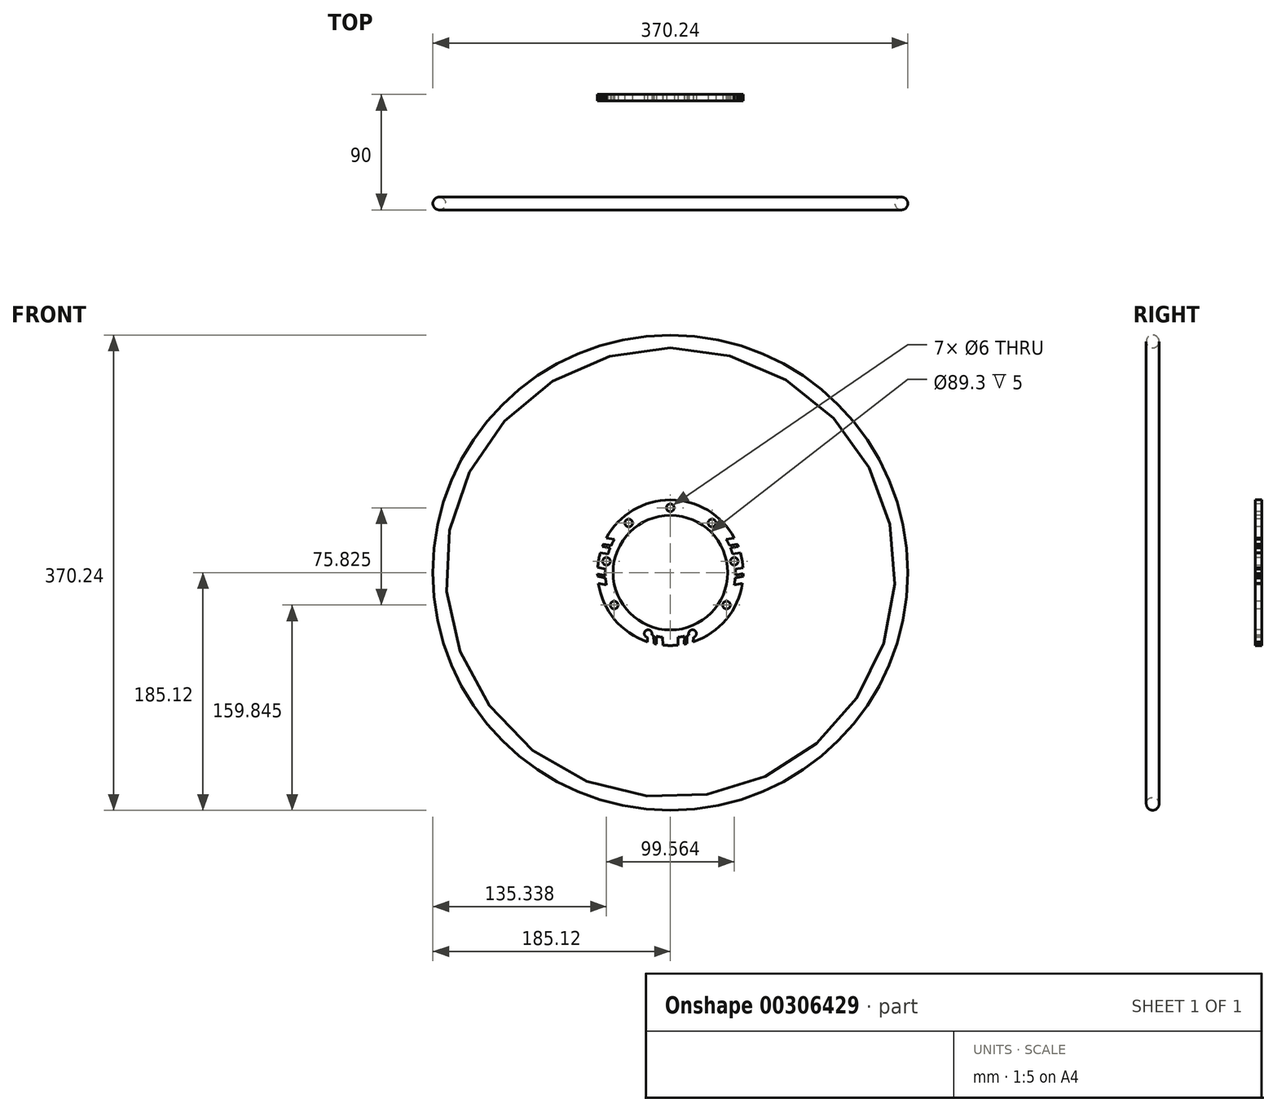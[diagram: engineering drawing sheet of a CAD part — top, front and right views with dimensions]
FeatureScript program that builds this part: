
annotation { "Feature Type Name" : "Feature", "Feature Type Description" : "" }
export const myFeature = defineFeature(function(context is Context, id is Id, definition is map)
    precondition{}
    {
        {
            var Q0;
            Q0=qCreatedBy(makeId("Front.planeOp"),FACE);
            var sketch = newSketch(context, id + "F0", { "sketchPlane" : qUnion([Q0])});
            skCircle(sketch, "E0", {"center": v(0, 0) * mm, "radius": 180 * mm});
            skCircle(sketch, "E1", {"center": v(0, 0) * mm, "radius": 44.65 * mm});
            skCircle(sketch, "E2", {"center": v(0, 50.55) * mm, "radius": 3 * mm});
            skCircle(sketch, "E3.1.0", {"center": v(32.5, 38.72) * mm, "radius": 3 * mm});
            skCircle(sketch, "E3.2.0", {"center": v(49.78, 8.78) * mm, "radius": 3 * mm});
            skLineSegment(sketch, "E3.anchor1", {"start": v(0, 0) * mm, "end": v(0, 50.55) * mm, "construction": true});
            skLineSegment(sketch, "E3.anchor2", {"start": v(0, 0) * mm, "end": v(-32.5, 38.72) * mm, "construction": true});
            skCircle(sketch, "E4.1.3.0", {"center": v(43.78, -25.28) * mm, "radius": 3 * mm});
            skCircle(sketch, "E4.1.4.0", {"center": v(17.29, -47.5) * mm, "radius": 3 * mm});
            skCircle(sketch, "E4.1.5.0", {"center": v(-17.29, -47.5) * mm, "radius": 3 * mm});
            skCircle(sketch, "E4.1.6.0", {"center": v(-43.78, -25.28) * mm, "radius": 3 * mm});
            skCircle(sketch, "E4.1.7.0", {"center": v(-49.78, 8.78) * mm, "radius": 3 * mm});
            skCircle(sketch, "E4.1.8.0", {"center": v(-32.5, 38.72) * mm, "radius": 3 * mm});
            skLineSegment(sketch, "E5", {"start": v(50.63, 2.67) * mm, "end": v(56.62, 3.9) * mm});
            skArc(sketch, "E6", {"start": v(-43.56, 25.94) * mm, "mid": v(-44.85, 23.65) * mm, "end": v(-46.01, 21.3) * mm});
            skArc(sketch, "E7.trimOffspring", {"start": v(-50.62, 2.76) * mm, "mid": v(-50.7, 0.27) * mm, "end": v(-50.65, -2.21) * mm});
            skArc(sketch, "E8.trimOffspring", {"start": v(-46.86, 19.36) * mm, "mid": v(-47.75, 17.04) * mm, "end": v(-48.53, 14.68) * mm});
            skArc(sketch, "E9.trimOffspring", {"start": v(-50.52, -4.32) * mm, "mid": v(-50.22, -6.93) * mm, "end": v(-49.8, -9.52) * mm});
            skArc(sketch, "E10", {"start": v(45.98, 21.35) * mm, "mid": v(44.82, 23.7) * mm, "end": v(43.53, 26) * mm});
            skArc(sketch, "E11.trimOffspring", {"start": v(50.66, -1.98) * mm, "mid": v(50.7, 0.34) * mm, "end": v(50.63, 2.67) * mm});
            skArc(sketch, "E12.trimOffspring", {"start": v(48.52, 14.7) * mm, "mid": v(47.73, 17.1) * mm, "end": v(46.81, 19.47) * mm});
            skArc(sketch, "E13.trimOffspring", {"start": v(49.81, -9.45) * mm, "mid": v(50.23, -6.86) * mm, "end": v(50.52, -4.25) * mm});
            skArc(sketch, "E14.trimOffspring", {"start": v(-14.5, -48.58) * mm, "mid": v(-13.75, -48.8) * mm, "end": v(-13, -49) * mm});
            skArc(sketch, "E15", {"start": v(6.06, -50.34) * mm, "mid": v(8.51, -49.98) * mm, "end": v(10.94, -49.5) * mm});
            skArc(sketch, "E16.trimOffspring", {"start": v(13, -49) * mm, "mid": v(13.75, -48.8) * mm, "end": v(14.5, -48.58) * mm});
            skArc(sketch, "E17.trimOffspring", {"start": v(-10.93, -49.5) * mm, "mid": v(-8.51, -49.98) * mm, "end": v(-6.07, -50.34) * mm});
            skLineSegment(sketch, "E18", {"start": v(44.82, 23.7) * mm, "end": v(174.77, 43.07) * mm});
            skLineSegment(sketch, "E19", {"start": v(47.73, 17.1) * mm, "end": v(176.31, 36.26) * mm});
            skLineSegment(sketch, "E20", {"start": v(50.7, 0.34) * mm, "end": v(178.06, 26.36) * mm});
            skLineSegment(sketch, "E21", {"start": v(50.23, -6.86) * mm, "end": v(178.95, 19.43) * mm});
            skLineSegment(sketch, "E22", {"start": v(8.51, -49.98) * mm, "end": v(5.15, -179.93) * mm});
            skLineSegment(sketch, "E23", {"start": v(-8.51, -49.98) * mm, "end": v(-5.41, -179.92) * mm});
            skLineSegment(sketch, "E24", {"start": v(15.36, -49.8) * mm, "end": v(12, -179.6) * mm});
            skLineSegment(sketch, "E25", {"start": v(-15.1, -49.55) * mm, "end": v(-12, -179.6) * mm});
            skLineSegment(sketch, "E26", {"start": v(-50.22, -6.93) * mm, "end": v(-178.89, 19.96) * mm});
            skLineSegment(sketch, "E27", {"start": v(-50.7, 0.27) * mm, "end": v(-177.98, 26.87) * mm});
            skLineSegment(sketch, "E28", {"start": v(-47.75, 17.04) * mm, "end": v(-176.2, 36.77) * mm});
            skPoint(sketch, "E29.startSnap0", {"position": v(-44.85, 23.65) * mm});
            skLineSegment(sketch, "E30", {"start": v(49.85, 27.12) * mm, "end": v(49.94, 26.95) * mm});
            skLineSegment(sketch, "E31", {"start": v(43.53, 26) * mm, "end": v(49.94, 26.95) * mm});
            skLineSegment(sketch, "E32", {"start": v(45.98, 21.35) * mm, "end": v(52.2, 22.28) * mm});
            skLineSegment(sketch, "E33", {"start": v(46.81, 19.47) * mm, "end": v(52.96, 20.38) * mm});
            skLineSegment(sketch, "E34", {"start": v(48.52, 14.7) * mm, "end": v(54.57, 15.6) * mm});
            skLineSegment(sketch, "E35", {"start": v(50.66, -1.98) * mm, "end": v(56.75, -0.74) * mm});
            skLineSegment(sketch, "E36", {"start": v(50.52, -4.25) * mm, "end": v(56.67, -3) * mm});
            skLineSegment(sketch, "E37", {"start": v(49.81, -9.45) * mm, "end": v(56.16, -8.15) * mm});
            skLineSegment(sketch, "E38", {"start": v(-43.56, 25.94) * mm, "end": v(-49.96, 26.92) * mm});
            skLineSegment(sketch, "E39", {"start": v(-46.01, 21.3) * mm, "end": v(-52.2, 22.24) * mm});
            skLineSegment(sketch, "E40", {"start": v(-46.86, 19.36) * mm, "end": v(-53, 20.3) * mm});
            skLineSegment(sketch, "E41", {"start": v(-48.53, 14.68) * mm, "end": v(-54.56, 15.6) * mm});
            skLineSegment(sketch, "E42", {"start": v(-50.65, -2.21) * mm, "end": v(-56.74, -0.94) * mm});
            skLineSegment(sketch, "E43", {"start": v(-50.62, 2.76) * mm, "end": v(-56.6, 4) * mm});
            skLineSegment(sketch, "E44", {"start": v(-50.52, -4.32) * mm, "end": v(-56.67, -3.03) * mm});
            skLineSegment(sketch, "E45", {"start": v(-49.8, -9.52) * mm, "end": v(-56.16, -8.2) * mm});
            skLineSegment(sketch, "E46", {"start": v(-44.85, 23.65) * mm, "end": v(-174.64, 43.58) * mm});
            skLineSegment(sketch, "E47", {"start": v(13, -49) * mm, "end": v(12.84, -55.28) * mm});
            skLineSegment(sketch, "E48", {"start": v(10.94, -49.5) * mm, "end": v(10.78, -55.72) * mm});
            skLineSegment(sketch, "E49", {"start": v(6.06, -50.34) * mm, "end": v(5.9, -56.44) * mm});
            skLineSegment(sketch, "E50", {"start": v(17.92, -50.43) * mm, "end": v(17.83, -53.88) * mm});
            skLineSegment(sketch, "E51", {"start": v(-6.07, -50.34) * mm, "end": v(-5.92, -56.44) * mm});
            skLineSegment(sketch, "E52", {"start": v(-10.93, -49.5) * mm, "end": v(-10.78, -55.72) * mm});
            skLineSegment(sketch, "E53", {"start": v(-13, -49) * mm, "end": v(-12.85, -55.28) * mm});
            skLineSegment(sketch, "E54", {"start": v(-17.92, -50.43) * mm, "end": v(-17.84, -53.87) * mm});
            skArc(sketch, "E55", {"start": v(49.94, 26.95) * mm, "mid": v(-0.02, 56.75) * mm, "end": v(-49.96, 26.92) * mm});
            skArc(sketch, "E56.trimOffspring", {"start": v(52.96, 20.38) * mm, "mid": v(52.59, 21.34) * mm, "end": v(52.2, 22.28) * mm});
            skArc(sketch, "E57.trimOffspring", {"start": v(56.67, -3) * mm, "mid": v(56.72, -1.87) * mm, "end": v(56.75, -0.74) * mm});
            skArc(sketch, "E58.trimOffspring", {"start": v(56.62, 3.9) * mm, "mid": v(55.9, 9.8) * mm, "end": v(54.57, 15.6) * mm});
            skArc(sketch, "E59.trimOffspring", {"start": v(-52.2, 22.24) * mm, "mid": v(-52.61, 21.28) * mm, "end": v(-53, 20.3) * mm});
            skArc(sketch, "E60.trimOffspring", {"start": v(-54.56, 15.6) * mm, "mid": v(-55.89, 9.86) * mm, "end": v(-56.6, 4) * mm});
            skArc(sketch, "E61.trimOffspring", {"start": v(-56.74, -0.94) * mm, "mid": v(-56.72, -1.98) * mm, "end": v(-56.67, -3.03) * mm});
            skArc(sketch, "E62.trimOffspring", {"start": v(-56.16, -8.2) * mm, "mid": v(-43.48, -36.47) * mm, "end": v(-17.84, -53.87) * mm});
            skArc(sketch, "E63.trimOffspring", {"start": v(-12.85, -55.28) * mm, "mid": v(-11.82, -55.5) * mm, "end": v(-10.78, -55.72) * mm});
            skArc(sketch, "E64.trimOffspring", {"start": v(-5.92, -56.44) * mm, "mid": v(-0.01, -56.75) * mm, "end": v(5.9, -56.44) * mm});
            skArc(sketch, "E65.trimOffspring", {"start": v(10.78, -55.72) * mm, "mid": v(11.81, -55.5) * mm, "end": v(12.84, -55.28) * mm});
            skArc(sketch, "E66.trimOffspring", {"start": v(17.83, -53.88) * mm, "mid": v(43.49, -36.46) * mm, "end": v(56.16, -8.15) * mm});
            skPoint(sketch, "E67.orphan", {"position": v(15.4, -48.58) * mm});
            skSolve(sketch);
        }
        {
            var Q0;
            Q0=qCreatedBy(makeId("Top.planeOp"),FACE);
            var sketch = newSketch(context, id + "F1", { "sketchPlane" : qUnion([Q0])});
            skCircle(sketch, "E68", {"center": v(-180.12, 0) * mm, "radius": 5 * mm});
            skSolve(sketch);
        }
        {
            var Q0;
            Q0=makeQuery(id+"F1.imprint","IMPRINT",FACE,{"disambiguationData":[TD([[makeQuery(id+"F1.imprint","IMPRINT",EDGE,{"derivedFrom":sQuery(id+"F1.wireOp",EDGE,"E68")}),1.0]])]});
            var Q1;
            Q1=sQuery(id+"F0.wireOp",EDGE,"E0");
            revolve(context, id + "F2", {"entities" : qUnion([Q0]), "axis" : qUnion([Q1]), "revolveType" : RevolveType.FULL});
        }
        {
            var Q0;
            Q0=makeQuery(id+"F0.imprint","IMPRINT",FACE,{"disambiguationData":[TD([[makeQuery(id+"F0.imprint","IMPRINT",EDGE,{"derivedFrom":sQuery(id+"F0.wireOp",EDGE,"E1")}),-1.0]])]});
            extrude(context, id + "F3", {"entities" : qUnion([Q0]), "oppositeDirection" : true, "depth" : 85 * mm, "offsetDistance" : 25 * mm, "hasSecondDirection" : true, "secondDirectionOppositeDirection" : true, "secondDirectionDepth" : 80 * mm});
        }
        {
            var Q0;
            Q0=sQuery(id+"F0.wireOp",EDGE,"E46");
            extrude(context, id + "F4", {"bodyType" : ToolBodyType.SURFACE, "surfaceEntities" : qUnion([Q0]), "oppositeDirection" : true, "depth" : 82.5 * mm, "offsetDistance" : 25 * mm});
        }
    });
